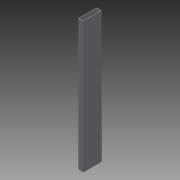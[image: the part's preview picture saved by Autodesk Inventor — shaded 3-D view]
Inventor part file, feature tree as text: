
AUTODESK INVENTOR PART (.ipt)
format: ipt  version: 2013 SP2 (Build 170200200, 200)  size: 71,168 bytes
history: native  units: mm
features: extrude x1, sketch x1
ambient origin geometry x8: Origin, YZ Plane, XZ Plane, XY Plane, X Axis, Y Axis, Z Axis, Center Point
bodies: Solid1 (feature_tree)
feature tree (2):
  extrude  "Extrusion1"  Depth=65.0mm
  sketch  "Sketch1"  dims[d0=18.0mm d1=65.0mm d2=1.5mm d3=459.0mm d4=0.0mm]
